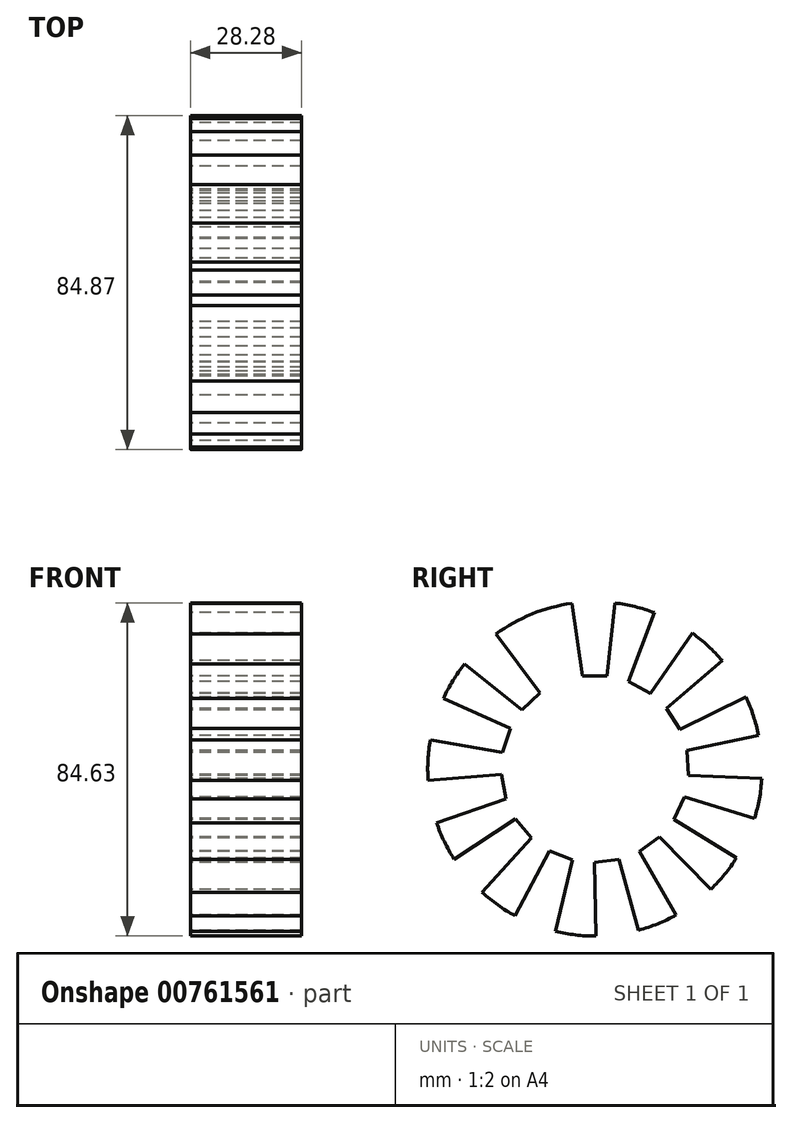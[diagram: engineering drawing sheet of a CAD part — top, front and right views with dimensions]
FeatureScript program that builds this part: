
annotation { "Feature Type Name" : "Feature", "Feature Type Description" : "" }
export const myFeature = defineFeature(function(context is Context, id is Id, definition is map)
    precondition{}
    {
        {
            var Q0;
            Q0=qCreatedBy(makeId("Front.planeOp"),FACE);
            var sketch = newSketch(context, id + "F0", { "sketchPlane" : qUnion([Q0])});
            skLineSegment(sketch, "E0.bottom", {"start": v(0, 0) * mm, "end": v(-28.28, 0) * mm});
            skLineSegment(sketch, "E0.top", {"start": v(0, 42.47) * mm, "end": v(-28.28, 42.47) * mm});
            skLineSegment(sketch, "E0.left", {"start": v(0, 0) * mm, "end": v(0, 42.47) * mm});
            skLineSegment(sketch, "E0.right", {"start": v(-28.28, 0) * mm, "end": v(-28.28, 42.47) * mm});
            skSolve(sketch);
        }
        {
            var Q0;
            Q0=makeQuery(id+"F0.imprint","IMPRINT",FACE,{"disambiguationData":[TD([[makeQuery(id+"F0.imprint","IMPRINT",EDGE,{"derivedFrom":sQuery(id+"F0.wireOp",EDGE,"E0.bottom")}),-1.0]])]});
            var Q1;
            Q1=sQuery(id+"F0.wireOp",EDGE,"E0.bottom");
            revolve(context, id + "F1", {"surfaceOperationType" : NewSurfaceOperationType.NEW, "entities" : qUnion([Q0]), "axis" : qUnion([Q1]), "revolveType" : RevolveType.FULL});
        }
        {
            var Q0;
            Q0=makeQuery(id+"F1.opRevolve","SWEPT_FACE",FACE,{"disambiguationData":[OSD([sQuery(id+"F0.wireOp",EDGE,"E0.right")])]});
            var sketch = newSketch(context, id + "F2", { "sketchPlane" : qUnion([Q0])});
            skLineSegment(sketch, "E1", {"start": v(-5.1, 42.16) * mm, "end": v(-3.1, 23.6) * mm});
            skLineSegment(sketch, "E2", {"start": v(-3.1, 23.6) * mm, "end": v(0, 23.6) * mm});
            skLineSegment(sketch, "E3", {"start": v(0, 23.6) * mm, "end": v(3.2, 23.6) * mm});
            skLineSegment(sketch, "E4", {"start": v(3.2, 23.6) * mm, "end": v(5.88, 42.06) * mm});
            skSolve(sketch);
        }
        {
            var Q0;
            {var subQ1=sQuery(id+"F2.wireOp",EDGE,"E1");Q0=makeQuery(id+"F2.imprint","IMPRINT",FACE,{"disambiguationData":[TD([[makeQuery(id+"F2.imprint","IMPRINT",EDGE,{"derivedFrom":subQ1}),1.0]])]});}
            extrude(context, id + "F3", {"entities" : qUnion([Q0]), "operationType" : NewBodyOperationType.REMOVE, "oppositeDirection" : true, "depth" : 50.8 * mm, "offsetDistance" : 25.4 * mm});
        }
        {
            var Q0;
            Q0=makeQuery(id+"F1.opRevolve","SWEPT_BODY",BODY,{"disambiguationData":[OSD([sQuery(id+"F0.wireOp",EDGE,"E0.bottom"),sQuery(id+"F0.wireOp",EDGE,"E0.top"),sQuery(id+"F0.wireOp",EDGE,"E0.left"),sQuery(id+"F0.wireOp",EDGE,"E0.right")])]});
            var Q1;
            Q1=makeQuery(id+"F3.boolean.opBoolean","COPY",FACE,{"derivedFrom":makeQuery(id+"F3.opExtrude","SWEPT_FACE",FACE,{"disambiguationData":[OSD([sQuery(id+"F2.wireOp",EDGE,"E1")])]})});
            var Q2;
            Q2=makeQuery(id+"F3.boolean.opBoolean","COPY",FACE,{"derivedFrom":makeQuery(id+"F3.opExtrude","SWEPT_FACE",FACE,{"disambiguationData":[OSD([sQuery(id+"F2.wireOp",EDGE,"E2"),sQuery(id+"F2.wireOp",EDGE,"E3")])]})});
            var Q3;
            Q3=makeQuery(id+"F3.boolean.opBoolean","COPY",FACE,{"derivedFrom":makeQuery(id+"F3.opExtrude","SWEPT_FACE",FACE,{"disambiguationData":[OSD([sQuery(id+"F2.wireOp",EDGE,"E4")])]})});
            var Q4;
            Q4=sQuery(id+"F0.wireOp",EDGE,"E0.bottom");
            circularPattern(context, id + "F4", {"patternType" : PatternType.FACE, "faces" : qUnion([Q1, Q2, Q3]), "axis" : qUnion([Q4]), "angle" : 360 * degree, "instanceCount" : 25, "equalSpace" : true});
        }
    });
